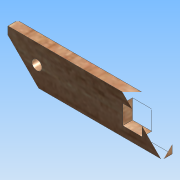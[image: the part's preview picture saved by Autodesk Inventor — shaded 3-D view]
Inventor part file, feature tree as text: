
AUTODESK INVENTOR PART (.ipt)
format: ipt  version: 2015 (Build 190159000, 159)  size: 115,200 bytes
history: native  units: mm
features: extrude x2, sketch x2, projected_geometry x1
ambient origin geometry x8: Origin, YZ Plane, XZ Plane, XY Plane, X Axis, Y Axis, Z Axis, Center Point
bodies: Body1 (feature_tree)
feature tree (5):
  extrude  "Extrusion2"  Depth=80.0mm
  extrude  "Extrusion3"  Depth=5.0mm TaperAngle=0.0deg
  sketch  "Sketch1"  dims[d2=20.0mm d3=80.0mm]
  sketch  "Sketch3"  dims[d4=5.2mm d5=5.0mm d6=0.0mm d7=15.0mm d8=10.0mm d11=10.0mm d12=10.0mm d14=10.0mm d15=0.0mm d17=64.5mm d18=10.0mm]
  projected_geometry  "Projected Loop1"
